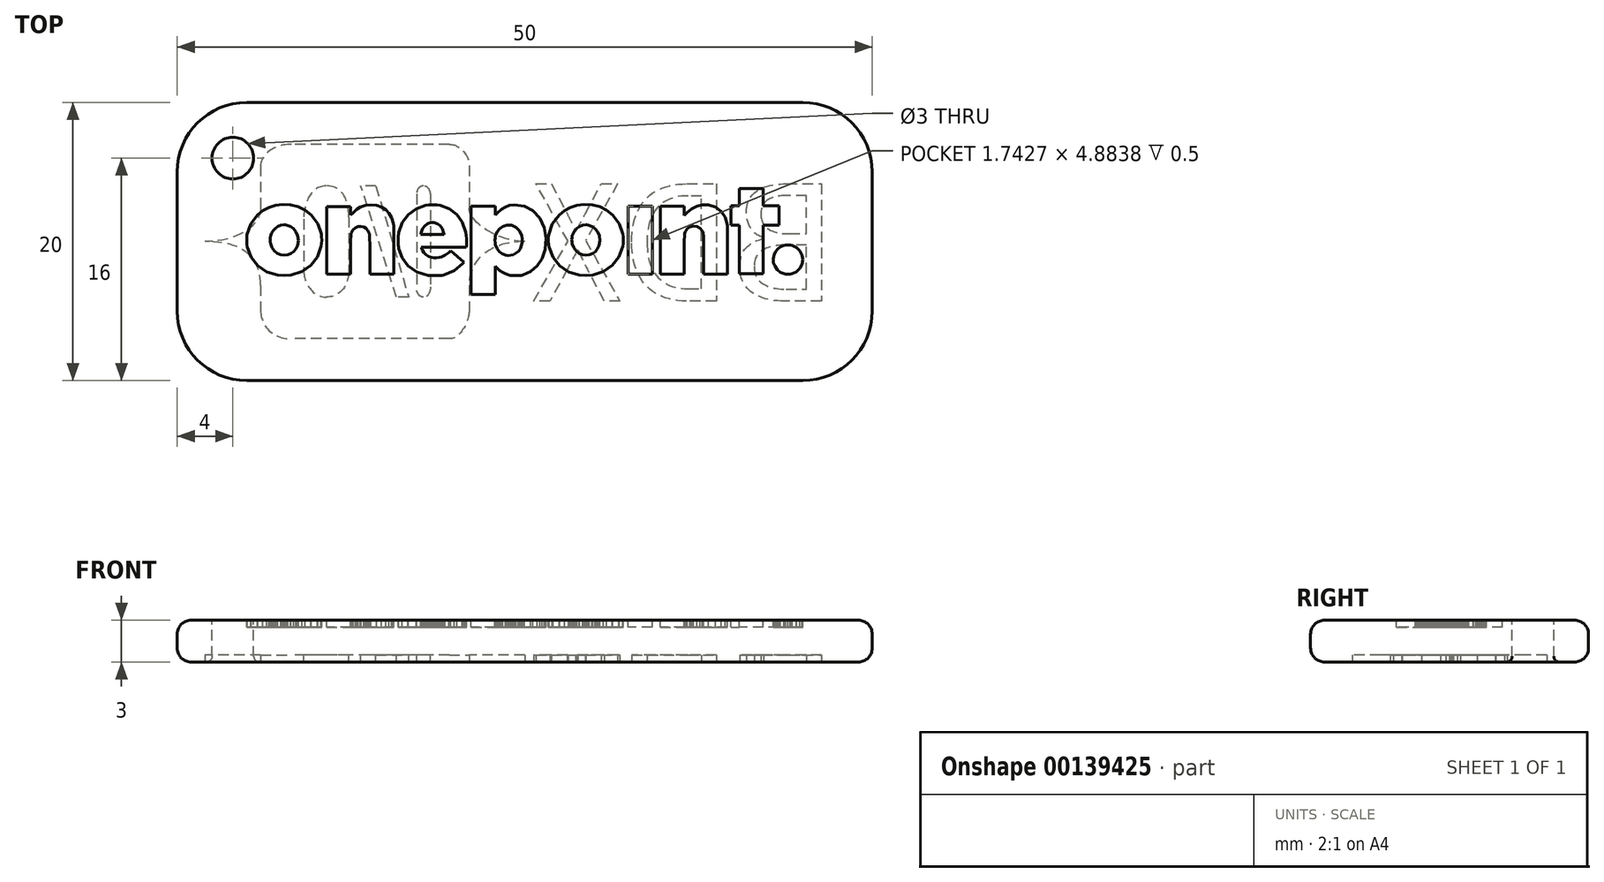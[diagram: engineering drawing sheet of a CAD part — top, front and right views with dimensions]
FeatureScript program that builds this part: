
annotation { "Feature Type Name" : "Feature", "Feature Type Description" : "" }
export const myFeature = defineFeature(function(context is Context, id is Id, definition is map)
    precondition{}
    {
        {
            var Q0;
            Q0=qCreatedBy(makeId("Top.planeOp"),FACE);
            var sketch = newSketch(context, id + "F0", { "sketchPlane" : qUnion([Q0])});
            skLineSegment(sketch, "E0.bottom", {"start": v(-25, 10) * mm, "end": v(25, 10) * mm});
            skLineSegment(sketch, "E0.top", {"start": v(-25, -10) * mm, "end": v(25, -10) * mm});
            skLineSegment(sketch, "E0.left", {"start": v(-25, 10) * mm, "end": v(-25, -10) * mm});
            skLineSegment(sketch, "E0.right", {"start": v(25, 10) * mm, "end": v(25, -10) * mm});
            skSolve(sketch);
        }
        {
            var Q0;
            Q0=qCreatedBy(makeId("Top.planeOp"),FACE);
            var sketch = newSketch(context, id + "F1", { "sketchPlane" : qUnion([Q0])});
            skLineSegment(sketch, "E1", {"start": v(-17.78, -2.42) * mm, "end": v(-18.55, -2.18) * mm});
            skLineSegment(sketch, "E2", {"start": v(-18.55, -2.18) * mm, "end": v(-19.2, -1.75) * mm});
            skLineSegment(sketch, "E3", {"start": v(-19.2, -1.75) * mm, "end": v(-19.67, -1.15) * mm});
            skLineSegment(sketch, "E4", {"start": v(-19.67, -1.15) * mm, "end": v(-19.95, -0.41) * mm});
            skLineSegment(sketch, "E5", {"start": v(-19.95, -0.41) * mm, "end": v(-19.99, -0.22) * mm});
            skLineSegment(sketch, "E6", {"start": v(-19.99, -0.22) * mm, "end": v(-20, 0.02) * mm});
            skLineSegment(sketch, "E7", {"start": v(-20, 0.02) * mm, "end": v(-20, 0.27) * mm});
            skLineSegment(sketch, "E8", {"start": v(-20, 0.27) * mm, "end": v(-19.98, 0.48) * mm});
            skLineSegment(sketch, "E9", {"start": v(-19.98, 0.48) * mm, "end": v(-19.72, 1.26) * mm});
            skLineSegment(sketch, "E10", {"start": v(-19.72, 1.26) * mm, "end": v(-19.22, 1.91) * mm});
            skLineSegment(sketch, "E11", {"start": v(-19.22, 1.91) * mm, "end": v(-18.84, 2.22) * mm});
            skLineSegment(sketch, "E12", {"start": v(-18.84, 2.22) * mm, "end": v(-18.41, 2.45) * mm});
            skLineSegment(sketch, "E13", {"start": v(-18.41, 2.45) * mm, "end": v(-17.94, 2.6) * mm});
            skLineSegment(sketch, "E14", {"start": v(-17.94, 2.6) * mm, "end": v(-17.43, 2.66) * mm});
            skLineSegment(sketch, "E15", {"start": v(-17.43, 2.66) * mm, "end": v(-16.85, 2.63) * mm});
            skLineSegment(sketch, "E16", {"start": v(-16.85, 2.63) * mm, "end": v(-16.3, 2.5) * mm});
            skLineSegment(sketch, "E17", {"start": v(-16.3, 2.5) * mm, "end": v(-15.8, 2.25) * mm});
            skLineSegment(sketch, "E18", {"start": v(-15.8, 2.25) * mm, "end": v(-15.37, 1.91) * mm});
            skLineSegment(sketch, "E19", {"start": v(-15.37, 1.91) * mm, "end": v(-14.89, 1.28) * mm});
            skLineSegment(sketch, "E20", {"start": v(-14.89, 1.28) * mm, "end": v(-14.63, 0.55) * mm});
            skLineSegment(sketch, "E21", {"start": v(-14.63, 0.55) * mm, "end": v(-14.61, 0.34) * mm});
            skLineSegment(sketch, "E22", {"start": v(-14.61, 0.34) * mm, "end": v(-14.6, 0.1) * mm});
            skLineSegment(sketch, "E23", {"start": v(-14.6, 0.1) * mm, "end": v(-14.62, -0.15) * mm});
            skLineSegment(sketch, "E24", {"start": v(-14.62, -0.15) * mm, "end": v(-14.65, -0.36) * mm});
            skLineSegment(sketch, "E25", {"start": v(-14.65, -0.36) * mm, "end": v(-14.92, -1.1) * mm});
            skLineSegment(sketch, "E26", {"start": v(-14.92, -1.1) * mm, "end": v(-15.39, -1.71) * mm});
            skLineSegment(sketch, "E27", {"start": v(-15.39, -1.71) * mm, "end": v(-16.03, -2.16) * mm});
            skLineSegment(sketch, "E28", {"start": v(-16.03, -2.16) * mm, "end": v(-16.8, -2.4) * mm});
            skLineSegment(sketch, "E29", {"start": v(-16.8, -2.4) * mm, "end": v(-17.3, -2.44) * mm});
            skLineSegment(sketch, "E30", {"start": v(-17.3, -2.44) * mm, "end": v(-17.78, -2.42) * mm});
            skLineSegment(sketch, "E31", {"start": v(-17.78, -2.42) * mm, "end": v(-17.78, -2.42) * mm});
            skLineSegment(sketch, "E32", {"start": v(-17.04, -0.95) * mm, "end": v(-16.81, -0.86) * mm});
            skLineSegment(sketch, "E33", {"start": v(-16.81, -0.86) * mm, "end": v(-16.62, -0.72) * mm});
            skLineSegment(sketch, "E34", {"start": v(-16.62, -0.72) * mm, "end": v(-16.47, -0.53) * mm});
            skLineSegment(sketch, "E35", {"start": v(-16.47, -0.53) * mm, "end": v(-16.35, -0.29) * mm});
            skLineSegment(sketch, "E36", {"start": v(-16.35, -0.29) * mm, "end": v(-16.3, 0.07) * mm});
            skLineSegment(sketch, "E37", {"start": v(-16.3, 0.07) * mm, "end": v(-16.33, 0.42) * mm});
            skLineSegment(sketch, "E38", {"start": v(-16.33, 0.42) * mm, "end": v(-16.46, 0.7) * mm});
            skLineSegment(sketch, "E39", {"start": v(-16.46, 0.7) * mm, "end": v(-16.63, 0.91) * mm});
            skLineSegment(sketch, "E40", {"start": v(-16.63, 0.91) * mm, "end": v(-16.86, 1.07) * mm});
            skLineSegment(sketch, "E41", {"start": v(-16.86, 1.07) * mm, "end": v(-17.12, 1.17) * mm});
            skLineSegment(sketch, "E42", {"start": v(-17.12, 1.17) * mm, "end": v(-17.23, 1.2) * mm});
            skLineSegment(sketch, "E43", {"start": v(-17.23, 1.2) * mm, "end": v(-17.32, 1.2) * mm});
            skLineSegment(sketch, "E44", {"start": v(-17.32, 1.2) * mm, "end": v(-17.54, 1.17) * mm});
            skLineSegment(sketch, "E45", {"start": v(-17.54, 1.17) * mm, "end": v(-17.76, 1.09) * mm});
            skLineSegment(sketch, "E46", {"start": v(-17.76, 1.09) * mm, "end": v(-17.94, 0.97) * mm});
            skLineSegment(sketch, "E47", {"start": v(-17.94, 0.97) * mm, "end": v(-18.1, 0.8) * mm});
            skLineSegment(sketch, "E48", {"start": v(-18.1, 0.8) * mm, "end": v(-18.2, 0.62) * mm});
            skLineSegment(sketch, "E49", {"start": v(-18.2, 0.62) * mm, "end": v(-18.28, 0.41) * mm});
            skLineSegment(sketch, "E50", {"start": v(-18.28, 0.41) * mm, "end": v(-18.3, 0.27) * mm});
            skLineSegment(sketch, "E51", {"start": v(-18.3, 0.27) * mm, "end": v(-18.32, 0.11) * mm});
            skLineSegment(sketch, "E52", {"start": v(-18.32, 0.11) * mm, "end": v(-18.3, -0.05) * mm});
            skLineSegment(sketch, "E53", {"start": v(-18.3, -0.05) * mm, "end": v(-18.28, -0.17) * mm});
            skLineSegment(sketch, "E54", {"start": v(-18.28, -0.17) * mm, "end": v(-18.18, -0.44) * mm});
            skLineSegment(sketch, "E55", {"start": v(-18.18, -0.44) * mm, "end": v(-18.01, -0.67) * mm});
            skLineSegment(sketch, "E56", {"start": v(-18.01, -0.67) * mm, "end": v(-17.8, -0.84) * mm});
            skLineSegment(sketch, "E57", {"start": v(-17.8, -0.84) * mm, "end": v(-17.55, -0.95) * mm});
            skLineSegment(sketch, "E58", {"start": v(-17.55, -0.95) * mm, "end": v(-17.3, -0.98) * mm});
            skLineSegment(sketch, "E59", {"start": v(-17.3, -0.98) * mm, "end": v(-17.04, -0.95) * mm});
            skLineSegment(sketch, "E60", {"start": v(-17.04, -0.95) * mm, "end": v(-17.04, -0.95) * mm});
            skLineSegment(sketch, "E61", {"start": v(-14.26, 0.08) * mm, "end": v(-14.26, 2.52) * mm});
            skLineSegment(sketch, "E62", {"start": v(-14.26, 2.52) * mm, "end": v(-12.53, 2.52) * mm});
            skLineSegment(sketch, "E63", {"start": v(-12.53, 2.52) * mm, "end": v(-12.53, 1.9) * mm});
            skLineSegment(sketch, "E64", {"start": v(-12.53, 1.9) * mm, "end": v(-12.34, 2.07) * mm});
            skLineSegment(sketch, "E65", {"start": v(-12.34, 2.07) * mm, "end": v(-12.09, 2.3) * mm});
            skLineSegment(sketch, "E66", {"start": v(-12.09, 2.3) * mm, "end": v(-11.81, 2.46) * mm});
            skLineSegment(sketch, "E67", {"start": v(-11.81, 2.46) * mm, "end": v(-11.46, 2.6) * mm});
            skLineSegment(sketch, "E68", {"start": v(-11.46, 2.6) * mm, "end": v(-11.07, 2.64) * mm});
            skLineSegment(sketch, "E69", {"start": v(-11.07, 2.64) * mm, "end": v(-10.67, 2.6) * mm});
            skLineSegment(sketch, "E70", {"start": v(-10.67, 2.6) * mm, "end": v(-10.3, 2.48) * mm});
            skLineSegment(sketch, "E71", {"start": v(-10.3, 2.48) * mm, "end": v(-10, 2.28) * mm});
            skLineSegment(sketch, "E72", {"start": v(-10, 2.28) * mm, "end": v(-9.75, 2.03) * mm});
            skLineSegment(sketch, "E73", {"start": v(-9.75, 2.03) * mm, "end": v(-9.57, 1.7) * mm});
            skLineSegment(sketch, "E74", {"start": v(-9.57, 1.7) * mm, "end": v(-9.45, 1.3) * mm});
            skLineSegment(sketch, "E75", {"start": v(-9.45, 1.3) * mm, "end": v(-9.44, 1.25) * mm});
            skLineSegment(sketch, "E76", {"start": v(-9.44, 1.25) * mm, "end": v(-9.43, 1.17) * mm});
            skLineSegment(sketch, "E77", {"start": v(-9.43, 1.17) * mm, "end": v(-9.43, 1.06) * mm});
            skLineSegment(sketch, "E78", {"start": v(-9.43, 1.06) * mm, "end": v(-9.42, 0.89) * mm});
            skLineSegment(sketch, "E79", {"start": v(-9.42, 0.89) * mm, "end": v(-9.42, 0.65) * mm});
            skLineSegment(sketch, "E80", {"start": v(-9.42, 0.65) * mm, "end": v(-9.41, 0.34) * mm});
            skLineSegment(sketch, "E81", {"start": v(-9.41, 0.34) * mm, "end": v(-9.41, -0.08) * mm});
            skLineSegment(sketch, "E82", {"start": v(-9.41, -0.08) * mm, "end": v(-9.4, -0.6) * mm});
            skLineSegment(sketch, "E83", {"start": v(-9.4, -0.6) * mm, "end": v(-9.4, -2.36) * mm});
            skLineSegment(sketch, "E84", {"start": v(-9.4, -2.36) * mm, "end": v(-11.14, -2.36) * mm});
            skLineSegment(sketch, "E85", {"start": v(-11.14, -2.36) * mm, "end": v(-11.14, -0.94) * mm});
            skLineSegment(sketch, "E86", {"start": v(-11.14, -0.94) * mm, "end": v(-11.14, -0.47) * mm});
            skLineSegment(sketch, "E87", {"start": v(-11.14, -0.47) * mm, "end": v(-11.15, -0.12) * mm});
            skLineSegment(sketch, "E88", {"start": v(-11.15, -0.12) * mm, "end": v(-11.15, 0.14) * mm});
            skLineSegment(sketch, "E89", {"start": v(-11.15, 0.14) * mm, "end": v(-11.15, 0.32) * mm});
            skLineSegment(sketch, "E90", {"start": v(-11.15, 0.32) * mm, "end": v(-11.16, 0.44) * mm});
            skLineSegment(sketch, "E91", {"start": v(-11.16, 0.44) * mm, "end": v(-11.16, 0.52) * mm});
            skLineSegment(sketch, "E92", {"start": v(-11.16, 0.52) * mm, "end": v(-11.17, 0.57) * mm});
            skLineSegment(sketch, "E93", {"start": v(-11.17, 0.57) * mm, "end": v(-11.19, 0.6) * mm});
            skLineSegment(sketch, "E94", {"start": v(-11.19, 0.6) * mm, "end": v(-11.28, 0.8) * mm});
            skLineSegment(sketch, "E95", {"start": v(-11.28, 0.8) * mm, "end": v(-11.4, 0.95) * mm});
            skLineSegment(sketch, "E96", {"start": v(-11.4, 0.95) * mm, "end": v(-11.56, 1.05) * mm});
            skLineSegment(sketch, "E97", {"start": v(-11.56, 1.05) * mm, "end": v(-11.76, 1.09) * mm});
            skLineSegment(sketch, "E98", {"start": v(-11.76, 1.09) * mm, "end": v(-11.99, 1.08) * mm});
            skLineSegment(sketch, "E99", {"start": v(-11.99, 1.08) * mm, "end": v(-12.2, 0.99) * mm});
            skLineSegment(sketch, "E100", {"start": v(-12.2, 0.99) * mm, "end": v(-12.36, 0.84) * mm});
            skLineSegment(sketch, "E101", {"start": v(-12.36, 0.84) * mm, "end": v(-12.48, 0.63) * mm});
            skLineSegment(sketch, "E102", {"start": v(-12.48, 0.63) * mm, "end": v(-12.5, 0.6) * mm});
            skLineSegment(sketch, "E103", {"start": v(-12.5, 0.6) * mm, "end": v(-12.5, 0.55) * mm});
            skLineSegment(sketch, "E104", {"start": v(-12.5, 0.55) * mm, "end": v(-12.5, 0.47) * mm});
            skLineSegment(sketch, "E105", {"start": v(-12.5, 0.47) * mm, "end": v(-12.51, 0.35) * mm});
            skLineSegment(sketch, "E106", {"start": v(-12.51, 0.35) * mm, "end": v(-12.52, 0.17) * mm});
            skLineSegment(sketch, "E107", {"start": v(-12.52, 0.17) * mm, "end": v(-12.52, -0.1) * mm});
            skLineSegment(sketch, "E108", {"start": v(-12.52, -0.1) * mm, "end": v(-12.52, -0.45) * mm});
            skLineSegment(sketch, "E109", {"start": v(-12.52, -0.45) * mm, "end": v(-12.53, -0.92) * mm});
            skLineSegment(sketch, "E110", {"start": v(-12.53, -0.92) * mm, "end": v(-12.53, -2.36) * mm});
            skLineSegment(sketch, "E111", {"start": v(-12.53, -2.36) * mm, "end": v(-14.26, -2.36) * mm});
            skLineSegment(sketch, "E112", {"start": v(-14.26, -2.36) * mm, "end": v(-14.26, 0.08) * mm});
            skLineSegment(sketch, "E113", {"start": v(-14.26, 0.08) * mm, "end": v(-14.26, 0.08) * mm});
            skLineSegment(sketch, "E114", {"start": v(-6.94, -2.44) * mm, "end": v(-7.76, -2.2) * mm});
            skLineSegment(sketch, "E115", {"start": v(-7.76, -2.2) * mm, "end": v(-8.4, -1.73) * mm});
            skLineSegment(sketch, "E116", {"start": v(-8.4, -1.73) * mm, "end": v(-8.83, -1.18) * mm});
            skLineSegment(sketch, "E117", {"start": v(-8.83, -1.18) * mm, "end": v(-9.06, -0.5) * mm});
            skLineSegment(sketch, "E118", {"start": v(-9.06, -0.5) * mm, "end": v(-9.08, -0.4) * mm});
            skLineSegment(sketch, "E119", {"start": v(-9.08, -0.4) * mm, "end": v(-9.1, -0.28) * mm});
            skLineSegment(sketch, "E120", {"start": v(-9.1, -0.28) * mm, "end": v(-9.1, -0.13) * mm});
            skLineSegment(sketch, "E121", {"start": v(-9.1, -0.13) * mm, "end": v(-9.1, 0.07) * mm});
            skLineSegment(sketch, "E122", {"start": v(-9.1, 0.07) * mm, "end": v(-9.1, 0.28) * mm});
            skLineSegment(sketch, "E123", {"start": v(-9.1, 0.28) * mm, "end": v(-9.1, 0.42) * mm});
            skLineSegment(sketch, "E124", {"start": v(-9.1, 0.42) * mm, "end": v(-9.08, 0.53) * mm});
            skLineSegment(sketch, "E125", {"start": v(-9.08, 0.53) * mm, "end": v(-9.06, 0.64) * mm});
            skLineSegment(sketch, "E126", {"start": v(-9.06, 0.64) * mm, "end": v(-8.8, 1.35) * mm});
            skLineSegment(sketch, "E127", {"start": v(-8.8, 1.35) * mm, "end": v(-8.38, 1.94) * mm});
            skLineSegment(sketch, "E128", {"start": v(-8.38, 1.94) * mm, "end": v(-7.81, 2.36) * mm});
            skLineSegment(sketch, "E129", {"start": v(-7.81, 2.36) * mm, "end": v(-7.13, 2.6) * mm});
            skLineSegment(sketch, "E130", {"start": v(-7.13, 2.6) * mm, "end": v(-6.9, 2.63) * mm});
            skLineSegment(sketch, "E131", {"start": v(-6.9, 2.63) * mm, "end": v(-6.6, 2.64) * mm});
            skLineSegment(sketch, "E132", {"start": v(-6.6, 2.64) * mm, "end": v(-6.32, 2.62) * mm});
            skLineSegment(sketch, "E133", {"start": v(-6.32, 2.62) * mm, "end": v(-6.08, 2.6) * mm});
            skLineSegment(sketch, "E134", {"start": v(-6.08, 2.6) * mm, "end": v(-5.41, 2.36) * mm});
            skLineSegment(sketch, "E135", {"start": v(-5.41, 2.36) * mm, "end": v(-4.88, 1.95) * mm});
            skLineSegment(sketch, "E136", {"start": v(-4.88, 1.95) * mm, "end": v(-4.5, 1.39) * mm});
            skLineSegment(sketch, "E137", {"start": v(-4.5, 1.39) * mm, "end": v(-4.25, 0.68) * mm});
            skLineSegment(sketch, "E138", {"start": v(-4.25, 0.68) * mm, "end": v(-4.22, 0.46) * mm});
            skLineSegment(sketch, "E139", {"start": v(-4.22, 0.46) * mm, "end": v(-4.2, 0.2) * mm});
            skLineSegment(sketch, "E140", {"start": v(-4.2, 0.2) * mm, "end": v(-4.18, -0.06) * mm});
            skLineSegment(sketch, "E141", {"start": v(-4.18, -0.06) * mm, "end": v(-4.18, -0.25) * mm});
            skLineSegment(sketch, "E142", {"start": v(-4.18, -0.25) * mm, "end": v(-4.2, -0.4) * mm});
            skLineSegment(sketch, "E143", {"start": v(-4.2, -0.4) * mm, "end": v(-7.45, -0.4) * mm});
            skLineSegment(sketch, "E144", {"start": v(-7.45, -0.4) * mm, "end": v(-7.43, -0.45) * mm});
            skLineSegment(sketch, "E145", {"start": v(-7.43, -0.45) * mm, "end": v(-7.41, -0.52) * mm});
            skLineSegment(sketch, "E146", {"start": v(-7.41, -0.52) * mm, "end": v(-7.36, -0.62) * mm});
            skLineSegment(sketch, "E147", {"start": v(-7.36, -0.62) * mm, "end": v(-7.25, -0.8) * mm});
            skLineSegment(sketch, "E148", {"start": v(-7.25, -0.8) * mm, "end": v(-7.1, -0.96) * mm});
            skLineSegment(sketch, "E149", {"start": v(-7.1, -0.96) * mm, "end": v(-6.91, -1.07) * mm});
            skLineSegment(sketch, "E150", {"start": v(-6.91, -1.07) * mm, "end": v(-6.7, -1.15) * mm});
            skLineSegment(sketch, "E151", {"start": v(-6.7, -1.15) * mm, "end": v(-6.53, -1.17) * mm});
            skLineSegment(sketch, "E152", {"start": v(-6.53, -1.17) * mm, "end": v(-6.33, -1.17) * mm});
            skLineSegment(sketch, "E153", {"start": v(-6.33, -1.17) * mm, "end": v(-6.14, -1.15) * mm});
            skLineSegment(sketch, "E154", {"start": v(-6.14, -1.15) * mm, "end": v(-5.98, -1.11) * mm});
            skLineSegment(sketch, "E155", {"start": v(-5.98, -1.11) * mm, "end": v(-5.72, -0.98) * mm});
            skLineSegment(sketch, "E156", {"start": v(-5.72, -0.98) * mm, "end": v(-5.46, -0.8) * mm});
            skLineSegment(sketch, "E157", {"start": v(-5.46, -0.8) * mm, "end": v(-5.32, -0.68) * mm});
            skLineSegment(sketch, "E158", {"start": v(-5.32, -0.68) * mm, "end": v(-4.84, -1.08) * mm});
            skLineSegment(sketch, "E159", {"start": v(-4.84, -1.08) * mm, "end": v(-4.36, -1.48) * mm});
            skLineSegment(sketch, "E160", {"start": v(-4.36, -1.48) * mm, "end": v(-4.45, -1.58) * mm});
            skLineSegment(sketch, "E161", {"start": v(-4.45, -1.58) * mm, "end": v(-5.07, -2.1) * mm});
            skLineSegment(sketch, "E162", {"start": v(-5.07, -2.1) * mm, "end": v(-5.83, -2.4) * mm});
            skLineSegment(sketch, "E163", {"start": v(-5.83, -2.4) * mm, "end": v(-5.95, -2.43) * mm});
            skLineSegment(sketch, "E164", {"start": v(-5.95, -2.43) * mm, "end": v(-6.06, -2.44) * mm});
            skLineSegment(sketch, "E165", {"start": v(-6.06, -2.44) * mm, "end": v(-6.22, -2.45) * mm});
            skLineSegment(sketch, "E166", {"start": v(-6.22, -2.45) * mm, "end": v(-6.44, -2.45) * mm});
            skLineSegment(sketch, "E167", {"start": v(-6.44, -2.45) * mm, "end": v(-6.6, -2.46) * mm});
            skLineSegment(sketch, "E168", {"start": v(-6.6, -2.46) * mm, "end": v(-6.75, -2.46) * mm});
            skLineSegment(sketch, "E169", {"start": v(-6.75, -2.46) * mm, "end": v(-6.87, -2.45) * mm});
            skLineSegment(sketch, "E170", {"start": v(-6.87, -2.45) * mm, "end": v(-6.94, -2.44) * mm});
            skLineSegment(sketch, "E171", {"start": v(-6.94, -2.44) * mm, "end": v(-6.94, -2.44) * mm});
            skLineSegment(sketch, "E172", {"start": v(-5.8, 0.53) * mm, "end": v(-5.82, 0.6) * mm});
            skLineSegment(sketch, "E173", {"start": v(-5.82, 0.6) * mm, "end": v(-5.85, 0.7) * mm});
            skLineSegment(sketch, "E174", {"start": v(-5.85, 0.7) * mm, "end": v(-5.89, 0.82) * mm});
            skLineSegment(sketch, "E175", {"start": v(-5.89, 0.82) * mm, "end": v(-5.93, 0.92) * mm});
            skLineSegment(sketch, "E176", {"start": v(-5.93, 0.92) * mm, "end": v(-6.08, 1.13) * mm});
            skLineSegment(sketch, "E177", {"start": v(-6.08, 1.13) * mm, "end": v(-6.28, 1.28) * mm});
            skLineSegment(sketch, "E178", {"start": v(-6.28, 1.28) * mm, "end": v(-6.52, 1.35) * mm});
            skLineSegment(sketch, "E179", {"start": v(-6.52, 1.35) * mm, "end": v(-6.77, 1.35) * mm});
            skLineSegment(sketch, "E180", {"start": v(-6.77, 1.35) * mm, "end": v(-7, 1.27) * mm});
            skLineSegment(sketch, "E181", {"start": v(-7, 1.27) * mm, "end": v(-7.2, 1.12) * mm});
            skLineSegment(sketch, "E182", {"start": v(-7.2, 1.12) * mm, "end": v(-7.34, 0.91) * mm});
            skLineSegment(sketch, "E183", {"start": v(-7.34, 0.91) * mm, "end": v(-7.45, 0.64) * mm});
            skLineSegment(sketch, "E184", {"start": v(-7.45, 0.64) * mm, "end": v(-7.48, 0.5) * mm});
            skLineSegment(sketch, "E185", {"start": v(-7.48, 0.5) * mm, "end": v(-6.64, 0.5) * mm});
            skLineSegment(sketch, "E186", {"start": v(-6.64, 0.5) * mm, "end": v(-6.4, 0.5) * mm});
            skLineSegment(sketch, "E187", {"start": v(-6.4, 0.5) * mm, "end": v(-6.2, 0.5) * mm});
            skLineSegment(sketch, "E188", {"start": v(-6.2, 0.5) * mm, "end": v(-6.05, 0.5) * mm});
            skLineSegment(sketch, "E189", {"start": v(-6.05, 0.5) * mm, "end": v(-5.94, 0.5) * mm});
            skLineSegment(sketch, "E190", {"start": v(-5.94, 0.5) * mm, "end": v(-5.87, 0.51) * mm});
            skLineSegment(sketch, "E191", {"start": v(-5.87, 0.51) * mm, "end": v(-5.83, 0.51) * mm});
            skLineSegment(sketch, "E192", {"start": v(-5.83, 0.51) * mm, "end": v(-5.81, 0.52) * mm});
            skLineSegment(sketch, "E193", {"start": v(-5.81, 0.52) * mm, "end": v(-5.8, 0.53) * mm});
            skLineSegment(sketch, "E194", {"start": v(-5.8, 0.53) * mm, "end": v(-5.8, 0.53) * mm});
            skLineSegment(sketch, "E195", {"start": v(-3.85, -0.63) * mm, "end": v(-3.85, 2.53) * mm});
            skLineSegment(sketch, "E196", {"start": v(-3.85, 2.53) * mm, "end": v(-2.12, 2.53) * mm});
            skLineSegment(sketch, "E197", {"start": v(-2.12, 2.53) * mm, "end": v(-2.12, 1.9) * mm});
            skLineSegment(sketch, "E198", {"start": v(-2.12, 1.9) * mm, "end": v(-1.95, 2.07) * mm});
            skLineSegment(sketch, "E199", {"start": v(-1.95, 2.07) * mm, "end": v(-1.68, 2.31) * mm});
            skLineSegment(sketch, "E200", {"start": v(-1.68, 2.31) * mm, "end": v(-1.4, 2.48) * mm});
            skLineSegment(sketch, "E201", {"start": v(-1.4, 2.48) * mm, "end": v(-1.09, 2.6) * mm});
            skLineSegment(sketch, "E202", {"start": v(-1.09, 2.6) * mm, "end": v(-0.74, 2.64) * mm});
            skLineSegment(sketch, "E203", {"start": v(-0.74, 2.64) * mm, "end": v(-0.03, 2.55) * mm});
            skLineSegment(sketch, "E204", {"start": v(-0.03, 2.55) * mm, "end": v(0.6, 2.22) * mm});
            skLineSegment(sketch, "E205", {"start": v(0.6, 2.22) * mm, "end": v(1.08, 1.7) * mm});
            skLineSegment(sketch, "E206", {"start": v(1.08, 1.7) * mm, "end": v(1.4, 1) * mm});
            skLineSegment(sketch, "E207", {"start": v(1.4, 1) * mm, "end": v(1.52, 0.22) * mm});
            skLineSegment(sketch, "E208", {"start": v(1.52, 0.22) * mm, "end": v(1.46, -0.58) * mm});
            skLineSegment(sketch, "E209", {"start": v(1.46, -0.58) * mm, "end": v(1.25, -1.23) * mm});
            skLineSegment(sketch, "E210", {"start": v(1.25, -1.23) * mm, "end": v(0.9, -1.76) * mm});
            skLineSegment(sketch, "E211", {"start": v(0.9, -1.76) * mm, "end": v(0.43, -2.16) * mm});
            skLineSegment(sketch, "E212", {"start": v(0.43, -2.16) * mm, "end": v(-0.13, -2.4) * mm});
            skLineSegment(sketch, "E213", {"start": v(-0.13, -2.4) * mm, "end": v(-0.25, -2.43) * mm});
            skLineSegment(sketch, "E214", {"start": v(-0.25, -2.43) * mm, "end": v(-0.35, -2.45) * mm});
            skLineSegment(sketch, "E215", {"start": v(-0.35, -2.45) * mm, "end": v(-0.47, -2.45) * mm});
            skLineSegment(sketch, "E216", {"start": v(-0.47, -2.45) * mm, "end": v(-0.64, -2.45) * mm});
            skLineSegment(sketch, "E217", {"start": v(-0.64, -2.45) * mm, "end": v(-0.81, -2.45) * mm});
            skLineSegment(sketch, "E218", {"start": v(-0.81, -2.45) * mm, "end": v(-0.94, -2.45) * mm});
            skLineSegment(sketch, "E219", {"start": v(-0.94, -2.45) * mm, "end": v(-1.04, -2.43) * mm});
            skLineSegment(sketch, "E220", {"start": v(-1.04, -2.43) * mm, "end": v(-1.14, -2.4) * mm});
            skLineSegment(sketch, "E221", {"start": v(-1.14, -2.4) * mm, "end": v(-1.37, -2.33) * mm});
            skLineSegment(sketch, "E222", {"start": v(-1.37, -2.33) * mm, "end": v(-1.58, -2.23) * mm});
            skLineSegment(sketch, "E223", {"start": v(-1.58, -2.23) * mm, "end": v(-1.78, -2.09) * mm});
            skLineSegment(sketch, "E224", {"start": v(-1.78, -2.09) * mm, "end": v(-1.98, -1.91) * mm});
            skLineSegment(sketch, "E225", {"start": v(-1.98, -1.91) * mm, "end": v(-2.12, -1.79) * mm});
            skLineSegment(sketch, "E226", {"start": v(-2.12, -1.79) * mm, "end": v(-2.12, -3.8) * mm});
            skLineSegment(sketch, "E227", {"start": v(-2.12, -3.8) * mm, "end": v(-3.85, -3.8) * mm});
            skLineSegment(sketch, "E228", {"start": v(-3.85, -3.8) * mm, "end": v(-3.85, -0.63) * mm});
            skLineSegment(sketch, "E229", {"start": v(-3.85, -0.63) * mm, "end": v(-3.85, -0.63) * mm});
            skLineSegment(sketch, "E230", {"start": v(-1, -1) * mm, "end": v(-0.8, -0.94) * mm});
            skLineSegment(sketch, "E231", {"start": v(-0.8, -0.94) * mm, "end": v(-0.61, -0.83) * mm});
            skLineSegment(sketch, "E232", {"start": v(-0.61, -0.83) * mm, "end": v(-0.44, -0.68) * mm});
            skLineSegment(sketch, "E233", {"start": v(-0.44, -0.68) * mm, "end": v(-0.32, -0.5) * mm});
            skLineSegment(sketch, "E234", {"start": v(-0.32, -0.5) * mm, "end": v(-0.23, -0.3) * mm});
            skLineSegment(sketch, "E235", {"start": v(-0.23, -0.3) * mm, "end": v(-0.19, -0.06) * mm});
            skLineSegment(sketch, "E236", {"start": v(-0.19, -0.06) * mm, "end": v(-0.18, 0.18) * mm});
            skLineSegment(sketch, "E237", {"start": v(-0.18, 0.18) * mm, "end": v(-0.22, 0.41) * mm});
            skLineSegment(sketch, "E238", {"start": v(-0.22, 0.41) * mm, "end": v(-0.38, 0.76) * mm});
            skLineSegment(sketch, "E239", {"start": v(-0.38, 0.76) * mm, "end": v(-0.63, 1.02) * mm});
            skLineSegment(sketch, "E240", {"start": v(-0.63, 1.02) * mm, "end": v(-0.94, 1.16) * mm});
            skLineSegment(sketch, "E241", {"start": v(-0.94, 1.16) * mm, "end": v(-1.3, 1.18) * mm});
            skLineSegment(sketch, "E242", {"start": v(-1.3, 1.18) * mm, "end": v(-1.57, 1.1) * mm});
            skLineSegment(sketch, "E243", {"start": v(-1.57, 1.1) * mm, "end": v(-1.8, 0.92) * mm});
            skLineSegment(sketch, "E244", {"start": v(-1.8, 0.92) * mm, "end": v(-1.99, 0.69) * mm});
            skLineSegment(sketch, "E245", {"start": v(-1.99, 0.69) * mm, "end": v(-2.1, 0.4) * mm});
            skLineSegment(sketch, "E246", {"start": v(-2.1, 0.4) * mm, "end": v(-2.13, 0.26) * mm});
            skLineSegment(sketch, "E247", {"start": v(-2.13, 0.26) * mm, "end": v(-2.14, 0.1) * mm});
            skLineSegment(sketch, "E248", {"start": v(-2.14, 0.1) * mm, "end": v(-2.13, -0.08) * mm});
            skLineSegment(sketch, "E249", {"start": v(-2.13, -0.08) * mm, "end": v(-2.1, -0.22) * mm});
            skLineSegment(sketch, "E250", {"start": v(-2.1, -0.22) * mm, "end": v(-2, -0.5) * mm});
            skLineSegment(sketch, "E251", {"start": v(-2, -0.5) * mm, "end": v(-1.83, -0.73) * mm});
            skLineSegment(sketch, "E252", {"start": v(-1.83, -0.73) * mm, "end": v(-1.61, -0.9) * mm});
            skLineSegment(sketch, "E253", {"start": v(-1.61, -0.9) * mm, "end": v(-1.36, -1) * mm});
            skLineSegment(sketch, "E254", {"start": v(-1.36, -1) * mm, "end": v(-1.19, -1.01) * mm});
            skLineSegment(sketch, "E255", {"start": v(-1.19, -1.01) * mm, "end": v(-1, -1) * mm});
            skLineSegment(sketch, "E256", {"start": v(7.43, 0.1) * mm, "end": v(7.43, 2.53) * mm});
            skLineSegment(sketch, "E257", {"start": v(7.43, 2.53) * mm, "end": v(9.18, 2.53) * mm});
            skLineSegment(sketch, "E258", {"start": v(9.18, 2.53) * mm, "end": v(9.18, -2.35) * mm});
            skLineSegment(sketch, "E259", {"start": v(9.18, -2.35) * mm, "end": v(7.43, -2.35) * mm});
            skLineSegment(sketch, "E260", {"start": v(7.43, -2.35) * mm, "end": v(7.43, 0.1) * mm});
            skLineSegment(sketch, "E261", {"start": v(3.93, -2.42) * mm, "end": v(3.15, -2.18) * mm});
            skLineSegment(sketch, "E262", {"start": v(3.15, -2.18) * mm, "end": v(2.5, -1.75) * mm});
            skLineSegment(sketch, "E263", {"start": v(2.5, -1.75) * mm, "end": v(2.03, -1.15) * mm});
            skLineSegment(sketch, "E264", {"start": v(2.03, -1.15) * mm, "end": v(1.75, -0.41) * mm});
            skLineSegment(sketch, "E265", {"start": v(1.75, -0.41) * mm, "end": v(1.72, -0.22) * mm});
            skLineSegment(sketch, "E266", {"start": v(1.72, -0.22) * mm, "end": v(1.7, 0.02) * mm});
            skLineSegment(sketch, "E267", {"start": v(1.7, 0.02) * mm, "end": v(1.7, 0.27) * mm});
            skLineSegment(sketch, "E268", {"start": v(1.7, 0.27) * mm, "end": v(1.73, 0.48) * mm});
            skLineSegment(sketch, "E269", {"start": v(1.73, 0.48) * mm, "end": v(1.98, 1.26) * mm});
            skLineSegment(sketch, "E270", {"start": v(1.98, 1.26) * mm, "end": v(2.48, 1.91) * mm});
            skLineSegment(sketch, "E271", {"start": v(2.48, 1.91) * mm, "end": v(2.86, 2.22) * mm});
            skLineSegment(sketch, "E272", {"start": v(2.86, 2.22) * mm, "end": v(3.3, 2.45) * mm});
            skLineSegment(sketch, "E273", {"start": v(3.3, 2.45) * mm, "end": v(3.76, 2.6) * mm});
            skLineSegment(sketch, "E274", {"start": v(3.76, 2.6) * mm, "end": v(4.27, 2.66) * mm});
            skLineSegment(sketch, "E275", {"start": v(4.27, 2.66) * mm, "end": v(4.86, 2.63) * mm});
            skLineSegment(sketch, "E276", {"start": v(4.86, 2.63) * mm, "end": v(5.4, 2.5) * mm});
            skLineSegment(sketch, "E277", {"start": v(5.4, 2.5) * mm, "end": v(5.9, 2.25) * mm});
            skLineSegment(sketch, "E278", {"start": v(5.9, 2.25) * mm, "end": v(6.33, 1.91) * mm});
            skLineSegment(sketch, "E279", {"start": v(6.33, 1.91) * mm, "end": v(6.81, 1.28) * mm});
            skLineSegment(sketch, "E280", {"start": v(6.81, 1.28) * mm, "end": v(7.07, 0.55) * mm});
            skLineSegment(sketch, "E281", {"start": v(7.07, 0.55) * mm, "end": v(7.1, 0.34) * mm});
            skLineSegment(sketch, "E282", {"start": v(7.1, 0.34) * mm, "end": v(7.1, 0.1) * mm});
            skLineSegment(sketch, "E283", {"start": v(7.1, 0.1) * mm, "end": v(7.08, -0.15) * mm});
            skLineSegment(sketch, "E284", {"start": v(7.08, -0.15) * mm, "end": v(7.06, -0.36) * mm});
            skLineSegment(sketch, "E285", {"start": v(7.06, -0.36) * mm, "end": v(6.79, -1.1) * mm});
            skLineSegment(sketch, "E286", {"start": v(6.79, -1.1) * mm, "end": v(6.31, -1.71) * mm});
            skLineSegment(sketch, "E287", {"start": v(6.31, -1.71) * mm, "end": v(5.67, -2.16) * mm});
            skLineSegment(sketch, "E288", {"start": v(5.67, -2.16) * mm, "end": v(4.9, -2.4) * mm});
            skLineSegment(sketch, "E289", {"start": v(4.9, -2.4) * mm, "end": v(4.4, -2.44) * mm});
            skLineSegment(sketch, "E290", {"start": v(4.4, -2.44) * mm, "end": v(3.93, -2.42) * mm});
            skLineSegment(sketch, "E291", {"start": v(4.66, -0.95) * mm, "end": v(4.9, -0.86) * mm});
            skLineSegment(sketch, "E292", {"start": v(4.9, -0.86) * mm, "end": v(5.08, -0.72) * mm});
            skLineSegment(sketch, "E293", {"start": v(5.08, -0.72) * mm, "end": v(5.23, -0.53) * mm});
            skLineSegment(sketch, "E294", {"start": v(5.23, -0.53) * mm, "end": v(5.35, -0.29) * mm});
            skLineSegment(sketch, "E295", {"start": v(5.35, -0.29) * mm, "end": v(5.41, 0.07) * mm});
            skLineSegment(sketch, "E296", {"start": v(5.41, 0.07) * mm, "end": v(5.37, 0.42) * mm});
            skLineSegment(sketch, "E297", {"start": v(5.37, 0.42) * mm, "end": v(5.25, 0.7) * mm});
            skLineSegment(sketch, "E298", {"start": v(5.25, 0.7) * mm, "end": v(5.07, 0.91) * mm});
            skLineSegment(sketch, "E299", {"start": v(5.07, 0.91) * mm, "end": v(4.84, 1.07) * mm});
            skLineSegment(sketch, "E300", {"start": v(4.84, 1.07) * mm, "end": v(4.58, 1.17) * mm});
            skLineSegment(sketch, "E301", {"start": v(4.58, 1.17) * mm, "end": v(4.47, 1.2) * mm});
            skLineSegment(sketch, "E302", {"start": v(4.47, 1.2) * mm, "end": v(4.38, 1.2) * mm});
            skLineSegment(sketch, "E303", {"start": v(4.38, 1.2) * mm, "end": v(4.17, 1.17) * mm});
            skLineSegment(sketch, "E304", {"start": v(4.17, 1.17) * mm, "end": v(3.94, 1.09) * mm});
            skLineSegment(sketch, "E305", {"start": v(3.94, 1.09) * mm, "end": v(3.76, 0.97) * mm});
            skLineSegment(sketch, "E306", {"start": v(3.76, 0.97) * mm, "end": v(3.61, 0.8) * mm});
            skLineSegment(sketch, "E307", {"start": v(3.61, 0.8) * mm, "end": v(3.5, 0.62) * mm});
            skLineSegment(sketch, "E308", {"start": v(3.5, 0.62) * mm, "end": v(3.42, 0.41) * mm});
            skLineSegment(sketch, "E309", {"start": v(3.42, 0.41) * mm, "end": v(3.4, 0.27) * mm});
            skLineSegment(sketch, "E310", {"start": v(3.4, 0.27) * mm, "end": v(3.39, 0.11) * mm});
            skLineSegment(sketch, "E311", {"start": v(3.39, 0.11) * mm, "end": v(3.4, -0.05) * mm});
            skLineSegment(sketch, "E312", {"start": v(3.4, -0.05) * mm, "end": v(3.42, -0.17) * mm});
            skLineSegment(sketch, "E313", {"start": v(3.42, -0.17) * mm, "end": v(3.52, -0.44) * mm});
            skLineSegment(sketch, "E314", {"start": v(3.52, -0.44) * mm, "end": v(3.69, -0.67) * mm});
            skLineSegment(sketch, "E315", {"start": v(3.69, -0.67) * mm, "end": v(3.9, -0.84) * mm});
            skLineSegment(sketch, "E316", {"start": v(3.9, -0.84) * mm, "end": v(4.16, -0.95) * mm});
            skLineSegment(sketch, "E317", {"start": v(4.16, -0.95) * mm, "end": v(4.4, -0.98) * mm});
            skLineSegment(sketch, "E318", {"start": v(4.4, -0.98) * mm, "end": v(4.66, -0.95) * mm});
            skLineSegment(sketch, "E319", {"start": v(4.66, -0.95) * mm, "end": v(4.66, -0.95) * mm});
            skLineSegment(sketch, "E320", {"start": v(9.75, 0.1) * mm, "end": v(9.75, 2.53) * mm});
            skLineSegment(sketch, "E321", {"start": v(9.75, 2.53) * mm, "end": v(11.48, 2.53) * mm});
            skLineSegment(sketch, "E322", {"start": v(11.48, 2.53) * mm, "end": v(11.48, 1.88) * mm});
            skLineSegment(sketch, "E323", {"start": v(11.48, 1.88) * mm, "end": v(11.66, 2.06) * mm});
            skLineSegment(sketch, "E324", {"start": v(11.66, 2.06) * mm, "end": v(12.01, 2.36) * mm});
            skLineSegment(sketch, "E325", {"start": v(12.01, 2.36) * mm, "end": v(12.38, 2.56) * mm});
            skLineSegment(sketch, "E326", {"start": v(12.38, 2.56) * mm, "end": v(12.79, 2.64) * mm});
            skLineSegment(sketch, "E327", {"start": v(12.79, 2.64) * mm, "end": v(13.22, 2.63) * mm});
            skLineSegment(sketch, "E328", {"start": v(13.22, 2.63) * mm, "end": v(13.74, 2.47) * mm});
            skLineSegment(sketch, "E329", {"start": v(13.74, 2.47) * mm, "end": v(14.15, 2.17) * mm});
            skLineSegment(sketch, "E330", {"start": v(14.15, 2.17) * mm, "end": v(14.43, 1.74) * mm});
            skLineSegment(sketch, "E331", {"start": v(14.43, 1.74) * mm, "end": v(14.58, 1.18) * mm});
            skLineSegment(sketch, "E332", {"start": v(14.58, 1.18) * mm, "end": v(14.59, 1) * mm});
            skLineSegment(sketch, "E333", {"start": v(14.59, 1) * mm, "end": v(14.6, 0.6) * mm});
            skLineSegment(sketch, "E334", {"start": v(14.6, 0.6) * mm, "end": v(14.6, 0.04) * mm});
            skLineSegment(sketch, "E335", {"start": v(14.6, 0.04) * mm, "end": v(14.6, -0.65) * mm});
            skLineSegment(sketch, "E336", {"start": v(14.6, -0.65) * mm, "end": v(14.6, -2.35) * mm});
            skLineSegment(sketch, "E337", {"start": v(14.6, -2.35) * mm, "end": v(12.87, -2.35) * mm});
            skLineSegment(sketch, "E338", {"start": v(12.87, -2.35) * mm, "end": v(12.87, -0.96) * mm});
            skLineSegment(sketch, "E339", {"start": v(12.87, -0.96) * mm, "end": v(12.87, -0.46) * mm});
            skLineSegment(sketch, "E340", {"start": v(12.87, -0.46) * mm, "end": v(12.87, -0.08) * mm});
            skLineSegment(sketch, "E341", {"start": v(12.87, -0.08) * mm, "end": v(12.86, 0.2) * mm});
            skLineSegment(sketch, "E342", {"start": v(12.86, 0.2) * mm, "end": v(12.86, 0.4) * mm});
            skLineSegment(sketch, "E343", {"start": v(12.86, 0.4) * mm, "end": v(12.84, 0.54) * mm});
            skLineSegment(sketch, "E344", {"start": v(12.84, 0.54) * mm, "end": v(12.82, 0.63) * mm});
            skLineSegment(sketch, "E345", {"start": v(12.82, 0.63) * mm, "end": v(12.8, 0.7) * mm});
            skLineSegment(sketch, "E346", {"start": v(12.8, 0.7) * mm, "end": v(12.76, 0.77) * mm});
            skLineSegment(sketch, "E347", {"start": v(12.76, 0.77) * mm, "end": v(12.6, 0.96) * mm});
            skLineSegment(sketch, "E348", {"start": v(12.6, 0.96) * mm, "end": v(12.4, 1.08) * mm});
            skLineSegment(sketch, "E349", {"start": v(12.4, 1.08) * mm, "end": v(12.15, 1.1) * mm});
            skLineSegment(sketch, "E350", {"start": v(12.15, 1.1) * mm, "end": v(11.9, 1.04) * mm});
            skLineSegment(sketch, "E351", {"start": v(11.9, 1.04) * mm, "end": v(11.7, 0.9) * mm});
            skLineSegment(sketch, "E352", {"start": v(11.7, 0.9) * mm, "end": v(11.57, 0.72) * mm});
            skLineSegment(sketch, "E353", {"start": v(11.57, 0.72) * mm, "end": v(11.54, 0.65) * mm});
            skLineSegment(sketch, "E354", {"start": v(11.54, 0.65) * mm, "end": v(11.52, 0.58) * mm});
            skLineSegment(sketch, "E355", {"start": v(11.52, 0.58) * mm, "end": v(11.5, 0.48) * mm});
            skLineSegment(sketch, "E356", {"start": v(11.5, 0.48) * mm, "end": v(11.5, 0.34) * mm});
            skLineSegment(sketch, "E357", {"start": v(11.5, 0.34) * mm, "end": v(11.49, 0.14) * mm});
            skLineSegment(sketch, "E358", {"start": v(11.49, 0.14) * mm, "end": v(11.48, -0.13) * mm});
            skLineSegment(sketch, "E359", {"start": v(11.48, -0.13) * mm, "end": v(11.48, -0.5) * mm});
            skLineSegment(sketch, "E360", {"start": v(11.48, -0.5) * mm, "end": v(11.48, -0.99) * mm});
            skLineSegment(sketch, "E361", {"start": v(11.48, -0.99) * mm, "end": v(11.48, -2.35) * mm});
            skLineSegment(sketch, "E362", {"start": v(11.48, -2.35) * mm, "end": v(9.75, -2.35) * mm});
            skLineSegment(sketch, "E363", {"start": v(9.75, -2.35) * mm, "end": v(9.75, 0.1) * mm});
            skLineSegment(sketch, "E364", {"start": v(9.75, 0.1) * mm, "end": v(9.75, 0.1) * mm});
            skLineSegment(sketch, "E365", {"start": v(15.44, -0.57) * mm, "end": v(15.44, 1.18) * mm});
            skLineSegment(sketch, "E366", {"start": v(15.44, 1.18) * mm, "end": v(14.85, 1.18) * mm});
            skLineSegment(sketch, "E367", {"start": v(14.85, 1.18) * mm, "end": v(14.85, 2.57) * mm});
            skLineSegment(sketch, "E368", {"start": v(14.85, 2.57) * mm, "end": v(15.44, 2.57) * mm});
            skLineSegment(sketch, "E369", {"start": v(15.44, 2.57) * mm, "end": v(15.44, 3.8) * mm});
            skLineSegment(sketch, "E370", {"start": v(15.44, 3.8) * mm, "end": v(17.17, 3.8) * mm});
            skLineSegment(sketch, "E371", {"start": v(17.17, 3.8) * mm, "end": v(17.17, 2.57) * mm});
            skLineSegment(sketch, "E372", {"start": v(17.17, 2.57) * mm, "end": v(18.3, 2.57) * mm});
            skLineSegment(sketch, "E373", {"start": v(18.3, 2.57) * mm, "end": v(18.3, 1.18) * mm});
            skLineSegment(sketch, "E374", {"start": v(18.3, 1.18) * mm, "end": v(17.17, 1.18) * mm});
            skLineSegment(sketch, "E375", {"start": v(17.17, 1.18) * mm, "end": v(17.17, -2.32) * mm});
            skLineSegment(sketch, "E376", {"start": v(17.17, -2.32) * mm, "end": v(15.44, -2.32) * mm});
            skLineSegment(sketch, "E377", {"start": v(15.44, -2.32) * mm, "end": v(15.44, -0.57) * mm});
            skLineSegment(sketch, "E378", {"start": v(18.67, -2.33) * mm, "end": v(18.4, -2.2) * mm});
            skLineSegment(sketch, "E379", {"start": v(18.4, -2.2) * mm, "end": v(18.17, -2.02) * mm});
            skLineSegment(sketch, "E380", {"start": v(18.17, -2.02) * mm, "end": v(18, -1.79) * mm});
            skLineSegment(sketch, "E381", {"start": v(18, -1.79) * mm, "end": v(17.9, -1.51) * mm});
            skLineSegment(sketch, "E382", {"start": v(17.9, -1.51) * mm, "end": v(17.9, -1.38) * mm});
            skLineSegment(sketch, "E383", {"start": v(17.9, -1.38) * mm, "end": v(17.9, -1.22) * mm});
            skLineSegment(sketch, "E384", {"start": v(17.9, -1.22) * mm, "end": v(17.91, -1.07) * mm});
            skLineSegment(sketch, "E385", {"start": v(17.91, -1.07) * mm, "end": v(17.95, -0.95) * mm});
            skLineSegment(sketch, "E386", {"start": v(17.95, -0.95) * mm, "end": v(18.06, -0.73) * mm});
            skLineSegment(sketch, "E387", {"start": v(18.06, -0.73) * mm, "end": v(18.21, -0.54) * mm});
            skLineSegment(sketch, "E388", {"start": v(18.21, -0.54) * mm, "end": v(18.4, -0.4) * mm});
            skLineSegment(sketch, "E389", {"start": v(18.4, -0.4) * mm, "end": v(18.65, -0.29) * mm});
            skLineSegment(sketch, "E390", {"start": v(18.65, -0.29) * mm, "end": v(18.78, -0.26) * mm});
            skLineSegment(sketch, "E391", {"start": v(18.78, -0.26) * mm, "end": v(18.95, -0.25) * mm});
            skLineSegment(sketch, "E392", {"start": v(18.95, -0.25) * mm, "end": v(19.11, -0.26) * mm});
            skLineSegment(sketch, "E393", {"start": v(19.11, -0.26) * mm, "end": v(19.24, -0.29) * mm});
            skLineSegment(sketch, "E394", {"start": v(19.24, -0.29) * mm, "end": v(19.56, -0.45) * mm});
            skLineSegment(sketch, "E395", {"start": v(19.56, -0.45) * mm, "end": v(19.8, -0.68) * mm});
            skLineSegment(sketch, "E396", {"start": v(19.8, -0.68) * mm, "end": v(19.95, -0.97) * mm});
            skLineSegment(sketch, "E397", {"start": v(19.95, -0.97) * mm, "end": v(20, -1.3) * mm});
            skLineSegment(sketch, "E398", {"start": v(20, -1.3) * mm, "end": v(19.94, -1.65) * mm});
            skLineSegment(sketch, "E399", {"start": v(19.94, -1.65) * mm, "end": v(19.78, -1.95) * mm});
            skLineSegment(sketch, "E400", {"start": v(19.78, -1.95) * mm, "end": v(19.53, -2.19) * mm});
            skLineSegment(sketch, "E401", {"start": v(19.53, -2.19) * mm, "end": v(19.22, -2.33) * mm});
            skLineSegment(sketch, "E402", {"start": v(19.22, -2.33) * mm, "end": v(19.1, -2.35) * mm});
            skLineSegment(sketch, "E403", {"start": v(19.1, -2.35) * mm, "end": v(18.94, -2.35) * mm});
            skLineSegment(sketch, "E404", {"start": v(18.94, -2.35) * mm, "end": v(18.79, -2.35) * mm});
            skLineSegment(sketch, "E405", {"start": v(18.79, -2.35) * mm, "end": v(18.67, -2.33) * mm});
            skLineSegment(sketch, "E406", {"start": v(18.67, -2.33) * mm, "end": v(18.67, -2.33) * mm});
            skSolve(sketch);
        }
        {
            var Q0;
            Q0=qSketchRegion(id+"F0",true);
            extrude(context, id + "F2", {"entities" : qUnion([Q0]), "oppositeDirection" : true, "depth" : 3 * mm});
        }
        {
            var Q0;
            Q0=makeQuery(id+"F2.opExtrude","SWEPT_EDGE",EDGE,{"disambiguationData":[OSD([sQuery(id+"F0.wireOp",EDGE,"E0.top"),sQuery(id+"F0.wireOp",EDGE,"E0.right")])]});
            var Q1;
            Q1=makeQuery(id+"F2.opExtrude","SWEPT_EDGE",EDGE,{"disambiguationData":[OSD([sQuery(id+"F0.wireOp",EDGE,"E0.bottom"),sQuery(id+"F0.wireOp",EDGE,"E0.right")])]});
            var Q2;
            Q2=makeQuery(id+"F2.opExtrude","SWEPT_EDGE",EDGE,{"disambiguationData":[OSD([sQuery(id+"F0.wireOp",EDGE,"E0.bottom"),sQuery(id+"F0.wireOp",EDGE,"E0.left")])]});
            var Q3;
            Q3=makeQuery(id+"F2.opExtrude","SWEPT_EDGE",EDGE,{"disambiguationData":[OSD([sQuery(id+"F0.wireOp",EDGE,"E0.top"),sQuery(id+"F0.wireOp",EDGE,"E0.left")])]});
            fillet(context, id + "F3", {"entities" : qUnion([Q0, Q1, Q2, Q3]), "radius" : 5 * mm, "tangentPropagation" : true, "allowEdgeOverflow" : false});
        }
        {
            var Q0;
            Q0=makeQuery(id+"F2.opExtrude","CAP_EDGE",EDGE,{"disambiguationData":[OSD([sQuery(id+"F0.wireOp",EDGE,"E0.bottom")])],"isStart":true});
            var Q1;
            Q1=makeQuery(id+"F2.opExtrude","CAP_EDGE",EDGE,{"disambiguationData":[OSD([sQuery(id+"F0.wireOp",EDGE,"E0.right")])],"isStart":false});
            fillet(context, id + "F4", {"entities" : qUnion([Q0, Q1]), "radius" : 1 * mm, "tangentPropagation" : true, "allowEdgeOverflow" : false});
        }
        {
            var Q0;
            Q0=qSketchRegion(id+"F1",true);
            extrude(context, id + "F5", {"entities" : qUnion([Q0]), "operationType" : NewBodyOperationType.REMOVE, "oppositeDirection" : true, "depth" : 0.5 * mm});
        }
        {
            var Q0;
            Q0=makeQuery(id+"F0.imprint","IMPRINT",FACE,{"disambiguationData":[TD([[makeQuery(id+"F0.imprint","IMPRINT",EDGE,{"derivedFrom":sQuery(id+"F0.wireOp",EDGE,"E0.bottom")}),-1.0]])]});
            var sketch = newSketch(context, id + "F6", { "sketchPlane" : qUnion([Q0])});
            skCircle(sketch, "E407", {"center": v(-21, 6) * mm, "radius": 1.5 * mm});
            skSolve(sketch);
        }
        {
            var Q0;
            Q0=qSketchRegion(id+"F6",true);
            extrude(context, id + "F7", {"entities" : qUnion([Q0]), "operationType" : NewBodyOperationType.REMOVE, "endBound" : BoundingType.THROUGH_ALL, "oppositeDirection" : true, "depth" : 25 * mm});
        }
        {
            var Q0;
            Q0=makeQuery(id+"F7.boolean.opBoolean","COPY",EDGE,{"derivedFrom":makeQuery(id+"F7.opExtrude","CAP_EDGE",EDGE,{"disambiguationData":[OSD([sQuery(id+"F6.wireOp",EDGE,"E407")])],"isStart":true})});
            var Q1;
            Q1=makeQuery(id+"F7.boolean.opBoolean","INTERSECT",EDGE,{"derivedFrom":[makeQuery(id+"F2.opExtrude","CAP_FACE",FACE,{"disambiguationData":[OSD([sQuery(id+"F0.wireOp",EDGE,"E0.bottom"),sQuery(id+"F0.wireOp",EDGE,"E0.top"),sQuery(id+"F0.wireOp",EDGE,"E0.left"),sQuery(id+"F0.wireOp",EDGE,"E0.right")])],"isStart":false}),makeQuery(id+"F7.opExtrude","SWEPT_FACE",FACE,{"disambiguationData":[OSD([sQuery(id+"F6.wireOp",EDGE,"E407")])]})]});
            fillet(context, id + "F8", {"entities" : qUnion([Q0, Q1]), "radius" : 0.4 * mm, "tangentPropagation" : true, "allowEdgeOverflow" : false});
        }
        {
            var Q0;
            Q0=makeQuery(id+"F2.opExtrude","CAP_FACE",FACE,{"disambiguationData":[OSD([sQuery(id+"F0.wireOp",EDGE,"E0.bottom"),sQuery(id+"F0.wireOp",EDGE,"E0.top"),sQuery(id+"F0.wireOp",EDGE,"E0.left"),sQuery(id+"F0.wireOp",EDGE,"E0.right")])],"isStart":false});
            var sketch = newSketch(context, id + "F9", { "sketchPlane" : qUnion([Q0])});
            skLineSegment(sketch, "E408.bottom", {"start": v(23, -7) * mm, "end": v(-23, -7) * mm});
            skLineSegment(sketch, "E408.top", {"start": v(23, 7) * mm, "end": v(-23, 7) * mm});
            skLineSegment(sketch, "E408.left", {"start": v(23, -7) * mm, "end": v(23, 7) * mm});
            skLineSegment(sketch, "E408.right", {"start": v(-23, -7) * mm, "end": v(-23, 7) * mm});
            skLineSegment(sketch, "E409.bottom", {"start": v(0, -7) * mm, "end": v(-23, -7) * mm});
            skLineSegment(sketch, "E409.top", {"start": v(0, 7) * mm, "end": v(-23, 7) * mm});
            skLineSegment(sketch, "E409.left", {"start": v(0, -7) * mm, "end": v(0, 7) * mm});
            skText(sketch, "E410", { "text": "BDX", "fontName": "NotoSansCJKjp-Regular.otf"});
            skLineSegment(sketch, "E411.bottom", {"start": v(-4, -7) * mm, "end": v(-19, -7) * mm});
            skLineSegment(sketch, "E411.top", {"start": v(-4, 7) * mm, "end": v(-19, 7) * mm});
            skLineSegment(sketch, "E411.left", {"start": v(-4, -7) * mm, "end": v(-4, 7) * mm});
            skLineSegment(sketch, "E411.right", {"start": v(-19, -7) * mm, "end": v(-19, 7) * mm});
            skLineSegment(sketch, "E412", {"start": v(-4, -2.42) * mm, "end": v(-19, -2.42) * mm});
            skLineSegment(sketch, "E413", {"start": v(-4, 3.15) * mm, "end": v(-19, 3.15) * mm});
            skLineSegment(sketch, "E414", {"start": v(-4, -5.44) * mm, "end": v(-19, -5.44) * mm});
            skLineSegment(sketch, "E415", {"start": v(-4, 4.96) * mm, "end": v(-19, 4.96) * mm});
            skLineSegment(sketch, "E416", {"start": v(-5.42, -7) * mm, "end": v(-5.42, 7) * mm});
            skLineSegment(sketch, "E417", {"start": v(-16.8, -7) * mm, "end": v(-16.8, 7) * mm});
            skFitSpline(sketch, "E418", {"points": [v(0, 0) * mm, v(-4, -2.42) * mm], "startDerivative": vector(-5.26, 0) * mm, "endDerivative": vector(0, -3.44) * mm});
            skFitSpline(sketch, "E419", {"points": [v(-5.42, -7) * mm, v(-4, -5.44) * mm], "startDerivative": vector(2.02, 0) * mm, "endDerivative": vector(0, 2.65) * mm});
            skFitSpline(sketch, "E420", {"points": [v(-16.8, -7) * mm, v(-19, -5.44) * mm], "startDerivative": vector(-3.2, 0) * mm, "endDerivative": vector(0, 2.75) * mm});
            skFitSpline(sketch, "E421", {"points": [v(-19, -2.42) * mm, v(-23, 0) * mm], "startDerivative": vector(0, 3.5) * mm, "endDerivative": vector(-7.63, 0) * mm});
            skFitSpline(sketch, "E422", {"points": [v(-19, 4.96) * mm, v(-16.8, 7) * mm], "startDerivative": vector(0, 2.94) * mm, "endDerivative": vector(4.37, 0) * mm});
            skFitSpline(sketch, "E423", {"points": [v(-4, 4.96) * mm, v(-5.42, 7) * mm], "startDerivative": vector(0, 2.37) * mm, "endDerivative": vector(-2.37, 0) * mm});
            skFitSpline(sketch, "E424", {"points": [v(0, 0) * mm, v(-4, 3.15) * mm], "startDerivative": vector(-5.26, 0) * mm, "endDerivative": vector(0, 7.16) * mm});
            skFitSpline(sketch, "E425", {"points": [v(-19, 3.15) * mm, v(-23, 0) * mm], "startDerivative": vector(0, -6.55) * mm, "endDerivative": vector(-7.63, 0) * mm});
            const initialGuessF9  = {"E410": [0.0225, 0.00428, -1, 0, 0.00828]};
            skSetInitialGuess(sketch, initialGuessF9);
            skSolve(sketch);
        }
        {
            var Q0;
            {var subQ0=sQuery(id+"F9.wireOp",EDGE,"E419");Q0=makeQuery(id+"F9.imprint","IMPRINT",FACE,{"disambiguationData":[TD([[makeQuery(id+"F9.imprint","IMPRINT",EDGE,{"derivedFrom":subQ0}),1.0]])]});}
            var Q1;
            {var subQ0=sQuery(id+"F9.wireOp",EDGE,"E416");var subQ5=sQuery(id+"F9.wireOp",EDGE,"E414");var subQ6=makeQuery(id+"F9.imprint","INTERSECT",VERTEX,{"derivedFrom":[subQ5,subQ0]});Q1=makeQuery(id+"F9.imprint","IMPRINT",FACE,{"disambiguationData":[TD([[makeQuery(id+"F9.imprint","IMPRINT",EDGE,{"disambiguationData":[TD([[subQ6,-1.0]])],"derivedFrom":subQ5}),1.0]])]});}
            var Q2;
            {var subQ0=sQuery(id+"F9.wireOp",EDGE,"E420");Q2=makeQuery(id+"F9.imprint","IMPRINT",FACE,{"disambiguationData":[TD([[makeQuery(id+"F9.imprint","IMPRINT",EDGE,{"derivedFrom":subQ0}),-1.0]])]});}
            var Q3;
            {var subQ0=sQuery(id+"F9.wireOp",EDGE,"E412");var subQ5=sQuery(id+"F9.wireOp",EDGE,"E417");var subQ6=makeQuery(id+"F9.imprint","INTERSECT",VERTEX,{"derivedFrom":[subQ0,subQ5]});Q3=makeQuery(id+"F9.imprint","IMPRINT",FACE,{"disambiguationData":[TD([[makeQuery(id+"F9.imprint","IMPRINT",EDGE,{"disambiguationData":[TD([[subQ6,1.0]])],"derivedFrom":subQ5}),1.0]])]});}
            var Q4;
            {var subQ0=sQuery(id+"F9.wireOp",EDGE,"E416");var subQ1=sQuery(id+"F9.wireOp",EDGE,"E412");var subQ2=makeQuery(id+"F9.imprint","INTERSECT",VERTEX,{"derivedFrom":[subQ1,subQ0]});Q4=makeQuery(id+"F9.imprint","IMPRINT",FACE,{"disambiguationData":[TD([[makeQuery(id+"F9.imprint","IMPRINT",EDGE,{"disambiguationData":[TD([[subQ2,-1.0]])],"derivedFrom":subQ1}),1.0]])]});}
            var Q5;
            {var subQ0=sQuery(id+"F9.wireOp",EDGE,"E412");var subQ5=sQuery(id+"F9.wireOp",EDGE,"E416");var subQ6=makeQuery(id+"F9.imprint","INTERSECT",VERTEX,{"derivedFrom":[subQ0,subQ5]});Q5=makeQuery(id+"F9.imprint","IMPRINT",FACE,{"disambiguationData":[TD([[makeQuery(id+"F9.imprint","IMPRINT",EDGE,{"disambiguationData":[TD([[subQ6,1.0]])],"derivedFrom":subQ5}),-1.0]])]});}
            var Q6;
            {var subQ0=sQuery(id+"F9.wireOp",EDGE,"E418");Q6=makeQuery(id+"F9.imprint","IMPRINT",FACE,{"disambiguationData":[TD([[makeQuery(id+"F9.imprint","IMPRINT",EDGE,{"derivedFrom":subQ0}),-1.0]])]});}
            var Q7;
            {var subQ0=sQuery(id+"F9.wireOp",EDGE,"E412");var subQ5=sQuery(id+"F9.wireOp",EDGE,"E416");var subQ7=makeQuery(id+"F9.imprint","INTERSECT",VERTEX,{"derivedFrom":[subQ0,subQ5]});Q7=makeQuery(id+"F9.imprint","IMPRINT",FACE,{"disambiguationData":[TD([[makeQuery(id+"F9.imprint","IMPRINT",EDGE,{"disambiguationData":[TD([[subQ7,-1.0]])],"derivedFrom":subQ5}),-1.0]])]});}
            var Q8;
            {var subQ0=sQuery(id+"F9.wireOp",EDGE,"E416");var subQ1=sQuery(id+"F9.wireOp",EDGE,"E412");var subQ2=makeQuery(id+"F9.imprint","INTERSECT",VERTEX,{"derivedFrom":[subQ1,subQ0]});Q8=makeQuery(id+"F9.imprint","IMPRINT",FACE,{"disambiguationData":[TD([[makeQuery(id+"F9.imprint","IMPRINT",EDGE,{"disambiguationData":[TD([[subQ2,-1.0]])],"derivedFrom":subQ1}),-1.0]])]});}
            var Q9;
            {var subQ0=sQuery(id+"F9.wireOp",EDGE,"E412");var subQ5=sQuery(id+"F9.wireOp",EDGE,"E417");var subQ6=makeQuery(id+"F9.imprint","INTERSECT",VERTEX,{"derivedFrom":[subQ0,subQ5]});Q9=makeQuery(id+"F9.imprint","IMPRINT",FACE,{"disambiguationData":[TD([[makeQuery(id+"F9.imprint","IMPRINT",EDGE,{"disambiguationData":[TD([[subQ6,-1.0]])],"derivedFrom":subQ5}),1.0]])]});}
            var Q10;
            {var subQ0=sQuery(id+"F9.wireOp",EDGE,"E421");Q10=makeQuery(id+"F9.imprint","IMPRINT",FACE,{"disambiguationData":[TD([[makeQuery(id+"F9.imprint","IMPRINT",EDGE,{"derivedFrom":subQ0}),-1.0]])]});}
            var Q11;
            {var subQ0=sQuery(id+"F9.wireOp",EDGE,"E413");var subQ5=sQuery(id+"F9.wireOp",EDGE,"E417");var subQ6=makeQuery(id+"F9.imprint","INTERSECT",VERTEX,{"derivedFrom":[subQ0,subQ5]});Q11=makeQuery(id+"F9.imprint","IMPRINT",FACE,{"disambiguationData":[TD([[makeQuery(id+"F9.imprint","IMPRINT",EDGE,{"disambiguationData":[TD([[subQ6,-1.0]])],"derivedFrom":subQ5}),1.0]])]});}
            var Q12;
            {var subQ0=sQuery(id+"F9.wireOp",EDGE,"E416");var subQ1=sQuery(id+"F9.wireOp",EDGE,"E413");var subQ2=makeQuery(id+"F9.imprint","INTERSECT",VERTEX,{"derivedFrom":[subQ1,subQ0]});Q12=makeQuery(id+"F9.imprint","IMPRINT",FACE,{"disambiguationData":[TD([[makeQuery(id+"F9.imprint","IMPRINT",EDGE,{"disambiguationData":[TD([[subQ2,-1.0]])],"derivedFrom":subQ1}),-1.0]])]});}
            var Q13;
            {var subQ0=sQuery(id+"F9.wireOp",EDGE,"E413");var subQ5=sQuery(id+"F9.wireOp",EDGE,"E416");var subQ7=makeQuery(id+"F9.imprint","INTERSECT",VERTEX,{"derivedFrom":[subQ0,subQ5]});Q13=makeQuery(id+"F9.imprint","IMPRINT",FACE,{"disambiguationData":[TD([[makeQuery(id+"F9.imprint","IMPRINT",EDGE,{"disambiguationData":[TD([[subQ7,-1.0]])],"derivedFrom":subQ5}),-1.0]])]});}
            var Q14;
            {var subQ0=sQuery(id+"F9.wireOp",EDGE,"E423");Q14=makeQuery(id+"F9.imprint","IMPRINT",FACE,{"disambiguationData":[TD([[makeQuery(id+"F9.imprint","IMPRINT",EDGE,{"derivedFrom":subQ0}),1.0]])]});}
            var Q15;
            {var subQ0=sQuery(id+"F9.wireOp",EDGE,"E416");var subQ5=sQuery(id+"F9.wireOp",EDGE,"E415");var subQ7=makeQuery(id+"F9.imprint","INTERSECT",VERTEX,{"derivedFrom":[subQ5,subQ0]});Q15=makeQuery(id+"F9.imprint","IMPRINT",FACE,{"disambiguationData":[TD([[makeQuery(id+"F9.imprint","IMPRINT",EDGE,{"disambiguationData":[TD([[subQ7,-1.0]])],"derivedFrom":subQ5}),-1.0]])]});}
            var Q16;
            {var subQ0=sQuery(id+"F9.wireOp",EDGE,"E422");Q16=makeQuery(id+"F9.imprint","IMPRINT",FACE,{"disambiguationData":[TD([[makeQuery(id+"F9.imprint","IMPRINT",EDGE,{"derivedFrom":subQ0}),-1.0]])]});}
            extrude(context, id + "F10", {"entities" : qUnion([Q0, Q1, Q2, Q3, Q4, Q5, Q6, Q7, Q8, Q9, Q10, Q11, Q12, Q13, Q14, Q15, Q16]), "operationType" : NewBodyOperationType.REMOVE, "oppositeDirection" : true, "depth" : 0.5 * mm});
        }
        {
            var Q0;
            Q0=makeQuery(id+"F9.imprint","IMPRINT",FACE,{"disambiguationData":[TD([[makeQuery(id+"F9.imprint","IMPRINT",EDGE,{"derivedFrom":sQuery(id+"F9.wireOp",EDGE,"E410.sketch_text.stroke-0")}),1.0]])]});
            var Q1;
            Q1=makeQuery(id+"F9.imprint","IMPRINT",FACE,{"disambiguationData":[TD([[makeQuery(id+"F9.imprint","IMPRINT",EDGE,{"derivedFrom":sQuery(id+"F9.wireOp",EDGE,"E410.sketch_text.stroke-18")}),1.0]])]});
            var Q2;
            Q2=makeQuery(id+"F9.imprint","IMPRINT",FACE,{"disambiguationData":[TD([[makeQuery(id+"F9.imprint","IMPRINT",EDGE,{"derivedFrom":sQuery(id+"F9.wireOp",EDGE,"E410.sketch_text.stroke-28")}),1.0]])]});
            extrude(context, id + "F11", {"entities" : qUnion([Q0, Q1, Q2]), "operationType" : NewBodyOperationType.REMOVE, "oppositeDirection" : true, "depth" : 0.5 * mm});
        }
        {
            var Q0;
            Q0=makeQuery(id+"F10.boolean.opBoolean","COPY",FACE,{"derivedFrom":makeQuery(id+"F10.opExtrude","CAP_FACE",FACE,{"disambiguationData":[OSD([sQuery(id+"F9.wireOp",EDGE,"E411.bottom"),sQuery(id+"F9.wireOp",EDGE,"E411.top"),sQuery(id+"F9.wireOp",EDGE,"E411.left"),sQuery(id+"F9.wireOp",EDGE,"E411.right"),sQuery(id+"F9.wireOp",EDGE,"E418"),sQuery(id+"F9.wireOp",EDGE,"E419"),sQuery(id+"F9.wireOp",EDGE,"E420"),sQuery(id+"F9.wireOp",EDGE,"E421"),sQuery(id+"F9.wireOp",EDGE,"E422"),sQuery(id+"F9.wireOp",EDGE,"E423"),sQuery(id+"F9.wireOp",EDGE,"E424"),sQuery(id+"F9.wireOp",EDGE,"E425")])],"isStart":false})});
            var sketch = newSketch(context, id + "F12", { "sketchPlane" : qUnion([Q0])});
            skLineSegment(sketch, "E426.bottom", {"start": v(-4, -4) * mm, "end": v(-19, -4) * mm});
            skLineSegment(sketch, "E426.top", {"start": v(-4, 4) * mm, "end": v(-19, 4) * mm});
            skLineSegment(sketch, "E426.left", {"start": v(-4, -4) * mm, "end": v(-4, 4) * mm});
            skLineSegment(sketch, "E426.right", {"start": v(-19, -4) * mm, "end": v(-19, 4) * mm});
            skLineSegment(sketch, "E427.bottom", {"start": v(-6.78, -4) * mm, "end": v(-7.78, -4) * mm});
            skLineSegment(sketch, "E427.top", {"start": v(-6.78, 4) * mm, "end": v(-7.78, 4) * mm});
            skLineSegment(sketch, "E427.left", {"start": v(-6.78, -4) * mm, "end": v(-6.78, 4) * mm});
            skLineSegment(sketch, "E427.right", {"start": v(-7.78, -4) * mm, "end": v(-7.78, 4) * mm});
            skLineSegment(sketch, "E428.bottom", {"start": v(-12.66, -4) * mm, "end": v(-15.9, -4) * mm});
            skLineSegment(sketch, "E428.top", {"start": v(-12.66, 4) * mm, "end": v(-15.9, 4) * mm});
            skLineSegment(sketch, "E428.left", {"start": v(-12.66, -4) * mm, "end": v(-12.66, 4) * mm});
            skLineSegment(sketch, "E428.right", {"start": v(-15.9, -4) * mm, "end": v(-15.9, 4) * mm});
            skLineSegment(sketch, "E429.bottom", {"start": v(-8.26, -4.64) * mm, "end": v(-11.87, -4.64) * mm});
            skLineSegment(sketch, "E429.top", {"start": v(-8.26, 4.8) * mm, "end": v(-11.87, 4.8) * mm});
            skLineSegment(sketch, "E429.left", {"start": v(-8.26, -4.64) * mm, "end": v(-8.26, 4.8) * mm});
            skLineSegment(sketch, "E429.right", {"start": v(-11.87, -4.64) * mm, "end": v(-11.87, 4.8) * mm});
            skFitSpline(sketch, "E430", {"points": [v(-6.78, -3.41) * mm, v(-7.28, -4) * mm], "startDerivative": vector(0, -0.81) * mm, "endDerivative": vector(-0.91, 0) * mm});
            skFitSpline(sketch, "E431", {"points": [v(-7.28, 4) * mm, v(-7.78, 3.43) * mm], "startDerivative": vector(-0.84, 0) * mm, "endDerivative": vector(0, -0.88) * mm});
            skFitSpline(sketch, "E432", {"points": [v(-7.28, -4) * mm, v(-7.78, -3.41) * mm], "startDerivative": vector(-0.91, 0) * mm, "endDerivative": vector(0, 1.04) * mm});
            skFitSpline(sketch, "E433", {"points": [v(-6.78, 3.27) * mm, v(-7.28, 4) * mm], "startDerivative": vector(0, 0.91) * mm, "endDerivative": vector(-1.03, 0) * mm});
            skFitSpline(sketch, "E434", {"points": [v(-12.66, 2.1) * mm, v(-14.28, 4) * mm], "startDerivative": vector(0, 3.06) * mm, "endDerivative": vector(-3.06, 0) * mm});
            skFitSpline(sketch, "E435", {"points": [v(-14.28, -4) * mm, v(-15.9, -1.62) * mm], "startDerivative": vector(-2.95, 0) * mm, "endDerivative": vector(0, 4.06) * mm});
            skFitSpline(sketch, "E436", {"points": [v(-15.9, 2.08) * mm, v(-14.28, 4) * mm], "startDerivative": vector(0, 2.24) * mm, "endDerivative": vector(3.28, 0) * mm});
            skFitSpline(sketch, "E437", {"points": [v(-12.66, -1.76) * mm, v(-14.28, -4) * mm], "startDerivative": vector(0, -2.98) * mm, "endDerivative": vector(-4, 0) * mm});
            skLineSegment(sketch, "E438", {"start": v(-10.9, -4.64) * mm, "end": v(-8.26, 4.33) * mm});
            skLineSegment(sketch, "E439", {"start": v(-8.26, 4.33) * mm, "end": v(-8.96, 4.8) * mm});
            skLineSegment(sketch, "E440", {"start": v(-8.96, 4.8) * mm, "end": v(-11.87, -4.25) * mm});
            skLineSegment(sketch, "E441", {"start": v(-11.87, -4.25) * mm, "end": v(-10.9, -4.64) * mm});
            skSolve(sketch);
        }
        {
            var Q0;
            {var subQ3=sQuery(id+"F12.wireOp",EDGE,"E430");Q0=makeQuery(id+"F12.imprint","IMPRINT",FACE,{"disambiguationData":[TD([[makeQuery(id+"F12.imprint","IMPRINT",EDGE,{"derivedFrom":subQ3}),-1.0]])]});}
            var Q1;
            {var subQ0=sQuery(id+"F12.wireOp",EDGE,"E438");var subQ1=sQuery(id+"F12.wireOp",EDGE,"E426.bottom");var subQ2=makeQuery(id+"F12.imprint","INTERSECT",VERTEX,{"derivedFrom":[subQ1,subQ0]});Q1=makeQuery(id+"F12.imprint","IMPRINT",FACE,{"disambiguationData":[TD([[makeQuery(id+"F12.imprint","IMPRINT",EDGE,{"disambiguationData":[TD([[subQ2,-1.0]])],"derivedFrom":subQ1}),-1.0]])]});}
            var Q2;
            {var subQ0=sQuery(id+"F12.wireOp",EDGE,"E434");Q2=makeQuery(id+"F12.imprint","IMPRINT",FACE,{"disambiguationData":[TD([[makeQuery(id+"F12.imprint","IMPRINT",EDGE,{"derivedFrom":subQ0}),1.0]])]});}
            extrude(context, id + "F13", {"entities" : qUnion([Q0, Q1, Q2]), "operationType" : NewBodyOperationType.ADD, "depth" : 0.5 * mm});
        }
    });
